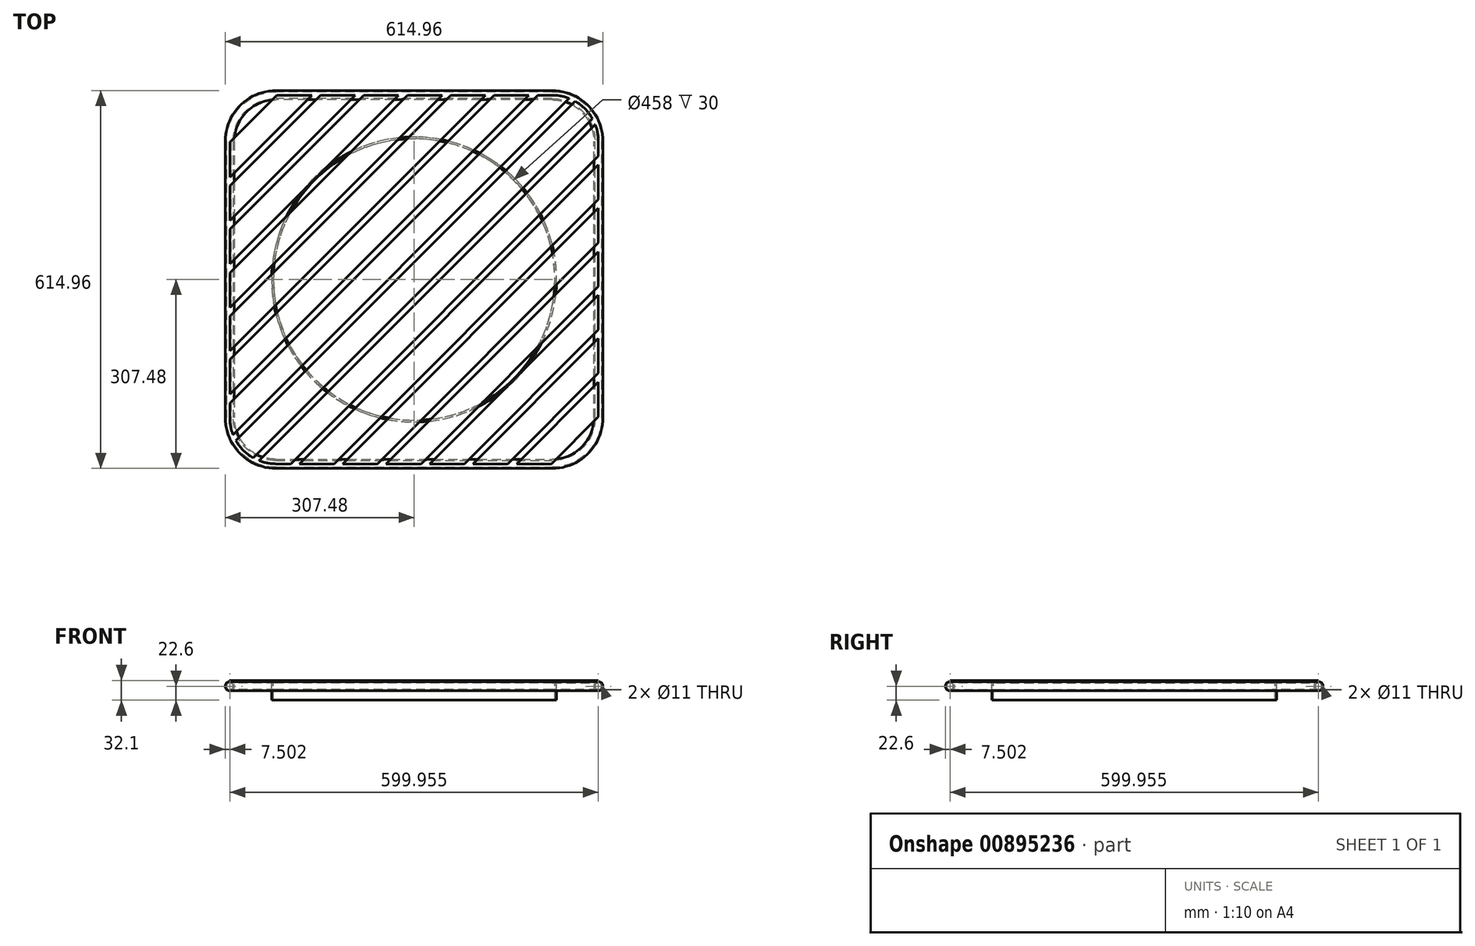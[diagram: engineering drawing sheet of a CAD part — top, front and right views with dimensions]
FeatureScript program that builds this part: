
annotation { "Feature Type Name" : "Feature", "Feature Type Description" : "" }
export const myFeature = defineFeature(function(context is Context, id is Id, definition is map)
    precondition{}
    {
        {
            var Q0;
            Q0=qCreatedBy(makeId("Top.planeOp"),FACE);
            var sketch = newSketch(context, id + "F0", { "sketchPlane" : qUnion([Q0])});
            skLineSegment(sketch, "E0.bottom", {"start": v(-225, 300) * mm, "end": v(225, 300) * mm});
            skLineSegment(sketch, "E0.top", {"start": v(-225, -300) * mm, "end": v(225, -300) * mm});
            skLineSegment(sketch, "E0.left", {"start": v(-300, 225) * mm, "end": v(-300, -225) * mm});
            skLineSegment(sketch, "E0.right", {"start": v(300, 225) * mm, "end": v(300, -225) * mm});
            skPoint(sketch, "E0.middle", {"position": v(0, 0) * mm});
            skArc(sketch, "E1", {"start": v(225, -300) * mm, "mid": v(278.03, -278.03) * mm, "end": v(300, -225) * mm});
            skPoint(sketch, "E2.orphan", {"position": v(300, -300) * mm});
            skArc(sketch, "E3", {"start": v(-300, -225) * mm, "mid": v(-278.03, -278.03) * mm, "end": v(-225, -300) * mm});
            skPoint(sketch, "E4.orphan", {"position": v(-300, -300) * mm});
            skArc(sketch, "E5.MirrorCS", {"start": v(225, 300) * mm, "mid": v(278.03, 278.03) * mm, "end": v(300, 225) * mm});
            skArc(sketch, "E6.MirrorCS", {"start": v(-300, 225) * mm, "mid": v(-278.03, 278.03) * mm, "end": v(-225, 300) * mm});
            skPoint(sketch, "E7.orphan", {"position": v(-300, 300) * mm});
            skPoint(sketch, "E8.orphan", {"position": v(300, 300) * mm});
            skSolve(sketch);
        }
        {
            var Q0;
            Q0=qCreatedBy(makeId("Front.planeOp"),FACE);
            var sketch = newSketch(context, id + "F1", { "sketchPlane" : qUnion([Q0])});
            skCircle(sketch, "E9", {"center": v(-299.98, 0) * mm, "radius": 7.5 * mm});
            skCircle(sketch, "E10", {"center": v(-299.98, 0) * mm, "radius": 5.5 * mm});
            skSolve(sketch);
        }
        {
            var Q0;
            Q0=makeQuery(id+"F1.imprint","IMPRINT",FACE,{"disambiguationData":[TD([[makeQuery(id+"F1.imprint","IMPRINT",EDGE,{"derivedFrom":sQuery(id+"F1.wireOp",EDGE,"E9")}),1.0]])]});
            var Q1;
            Q1=sQuery(id+"F0.wireOp",EDGE,"E3");
            var Q2;
            Q2=sQuery(id+"F0.wireOp",EDGE,"E0.left");
            var Q3;
            Q3=sQuery(id+"F0.wireOp",EDGE,"E6.MirrorCS");
            var Q4;
            Q4=sQuery(id+"F0.wireOp",EDGE,"E0.bottom");
            var Q5;
            Q5=sQuery(id+"F0.wireOp",EDGE,"E5.MirrorCS");
            var Q6;
            Q6=sQuery(id+"F0.wireOp",EDGE,"E0.right");
            var Q7;
            Q7=sQuery(id+"F0.wireOp",EDGE,"E1");
            var Q8;
            Q8=sQuery(id+"F0.wireOp",EDGE,"E0.top");
            sweep(context, id + "F2", {"profiles" : qUnion([Q0]), "path" : qUnion([Q1, Q2, Q3, Q4, Q5, Q6, Q7, Q8])});
        }
        {
            var Q0;
            Q0=qCreatedBy(makeId("Top.planeOp"),FACE);
            cPlane(context, id + "F3", {"entities" : qUnion([Q0]), "cplaneType" : CPlaneType.OFFSET, "offset" : 7.5 * mm, "width" : 150 * mm, "height" : 150 * mm});
        }
        {
            var Q0;
            Q0=qCreatedBy(id+"F3.planeOp",FACE);
            var sketch = newSketch(context, id + "F4", { "sketchPlane" : qUnion([Q0])});
            skLineSegment(sketch, "E11.bottom", {"start": v(-225, 300) * mm, "end": v(225, 300) * mm});
            skLineSegment(sketch, "E11.top", {"start": v(-225, -300) * mm, "end": v(225, -300) * mm});
            skLineSegment(sketch, "E11.left", {"start": v(-300, 225) * mm, "end": v(-300, -225) * mm});
            skLineSegment(sketch, "E11.right", {"start": v(300, 225) * mm, "end": v(300, -225) * mm});
            skPoint(sketch, "E11.middle", {"position": v(0, 0) * mm});
            skArc(sketch, "E12", {"start": v(-225, 300) * mm, "mid": v(-278.03, 278.03) * mm, "end": v(-300, 225) * mm});
            skArc(sketch, "E13", {"start": v(300, 225) * mm, "mid": v(278.03, 278.03) * mm, "end": v(225, 300) * mm});
            skPoint(sketch, "E14.orphan", {"position": v(-300, 300) * mm});
            skPoint(sketch, "E15.orphan", {"position": v(300, 300) * mm});
            skArc(sketch, "E16.MirrorCS", {"start": v(-225, -300) * mm, "mid": v(-278.03, -278.03) * mm, "end": v(-300, -225) * mm});
            skArc(sketch, "E17.MirrorCS", {"start": v(300, -225) * mm, "mid": v(278.03, -278.03) * mm, "end": v(225, -300) * mm});
            skPoint(sketch, "E18.orphan", {"position": v(-300, -300) * mm});
            skPoint(sketch, "E19.orphan", {"position": v(300, -300) * mm});
            skLineSegment(sketch, "E20", {"start": v(-300, 11.13) * mm, "end": v(-11.13, 300) * mm});
            skLineSegment(sketch, "E21", {"start": v(45.44, 300) * mm, "end": v(-300, -45.44) * mm});
            skLineSegment(sketch, "E22", {"start": v(59.58, 300) * mm, "end": v(-300, -59.58) * mm});
            skLineSegment(sketch, "E23", {"start": v(116.15, 300) * mm, "end": v(-300, -116.15) * mm});
            skLineSegment(sketch, "E24", {"start": v(130.3, 300) * mm, "end": v(-300, -130.3) * mm});
            skLineSegment(sketch, "E25", {"start": v(186.86, 300) * mm, "end": v(-300, -186.86) * mm});
            skLineSegment(sketch, "E26", {"start": v(201, 300) * mm, "end": v(-300, -201) * mm});
            skLineSegment(sketch, "E27", {"start": v(257.57, 300) * mm, "end": v(-300, -257.57) * mm});
            skLineSegment(sketch, "E28", {"start": v(-290.25, -261.97) * mm, "end": v(261.97, 290.25) * mm});
            skLineSegment(sketch, "E29.MirrorCS", {"start": v(-261.97, -290.25) * mm, "end": v(290.25, 261.97) * mm});
            skLineSegment(sketch, "E30.MirrorCS", {"start": v(294.82, 252.4) * mm, "end": v(-252.4, -294.82) * mm});
            skLineSegment(sketch, "E31.MirrorCS", {"start": v(300, 201) * mm, "end": v(-201, -300) * mm});
            skLineSegment(sketch, "E32.MirrorCS", {"start": v(300, 186.86) * mm, "end": v(-186.86, -300) * mm});
            skLineSegment(sketch, "E33.MirrorCS", {"start": v(300, 130.3) * mm, "end": v(-130.3, -300) * mm});
            skLineSegment(sketch, "E34.MirrorCS", {"start": v(300, 116.15) * mm, "end": v(-116.15, -300) * mm});
            skLineSegment(sketch, "E35.MirrorCS", {"start": v(300, 59.58) * mm, "end": v(-59.58, -300) * mm});
            skLineSegment(sketch, "E36.MirrorCS", {"start": v(300, 45.44) * mm, "end": v(-45.44, -300) * mm});
            skLineSegment(sketch, "E37.MirrorCS", {"start": v(11.13, -300) * mm, "end": v(300, -11.13) * mm});
            skLineSegment(sketch, "E38", {"start": v(300, -25.27) * mm, "end": v(25.27, -300) * mm});
            skLineSegment(sketch, "E39", {"start": v(300, -81.84) * mm, "end": v(81.84, -300) * mm});
            skLineSegment(sketch, "E40", {"start": v(300, -95.98) * mm, "end": v(95.98, -300) * mm});
            skLineSegment(sketch, "E41", {"start": v(-225, -225) * mm, "end": v(225, 225) * mm});
            skLineSegment(sketch, "E42", {"start": v(300, -152.55) * mm, "end": v(152.55, -300) * mm});
            skLineSegment(sketch, "E43.MirrorCS", {"start": v(-152.55, 300) * mm, "end": v(-300, 152.55) * mm});
            skLineSegment(sketch, "E44.MirrorCS", {"start": v(-95.98, 300) * mm, "end": v(-300, 95.98) * mm});
            skLineSegment(sketch, "E45.MirrorCS", {"start": v(-81.84, 300) * mm, "end": v(-300, 81.84) * mm});
            skLineSegment(sketch, "E46.MirrorCS", {"start": v(-25.27, 300) * mm, "end": v(-300, 25.27) * mm});
            skLineSegment(sketch, "E47", {"start": v(-166.7, 300) * mm, "end": v(-300, 166.7) * mm});
            skLineSegment(sketch, "E48", {"start": v(-223.26, 300) * mm, "end": v(-300, 223.26) * mm});
            skLineSegment(sketch, "E49.MirrorCS", {"start": v(300, -166.7) * mm, "end": v(166.7, -300) * mm});
            skLineSegment(sketch, "E50.MirrorCS", {"start": v(300, -223.26) * mm, "end": v(223.26, -300) * mm});
            skSolve(sketch);
        }
        {
            var Q0;
            {var subQ0=sQuery(id+"F4.wireOp",EDGE,"E20");Q0=makeQuery(id+"F4.imprint","IMPRINT",FACE,{"disambiguationData":[TD([[makeQuery(id+"F4.imprint","IMPRINT",EDGE,{"derivedFrom":subQ0}),-1.0]])]});}
            var Q1;
            {var subQ0=sQuery(id+"F4.wireOp",EDGE,"E22");Q1=makeQuery(id+"F4.imprint","IMPRINT",FACE,{"disambiguationData":[TD([[makeQuery(id+"F4.imprint","IMPRINT",EDGE,{"derivedFrom":subQ0}),1.0]])]});}
            var Q2;
            {var subQ0=sQuery(id+"F4.wireOp",EDGE,"E24");Q2=makeQuery(id+"F4.imprint","IMPRINT",FACE,{"disambiguationData":[TD([[makeQuery(id+"F4.imprint","IMPRINT",EDGE,{"derivedFrom":subQ0}),1.0]])]});}
            var Q3;
            {var subQ0=sQuery(id+"F4.wireOp",EDGE,"E26");Q3=makeQuery(id+"F4.imprint","IMPRINT",FACE,{"disambiguationData":[TD([[makeQuery(id+"F4.imprint","IMPRINT",EDGE,{"derivedFrom":subQ0}),1.0]])]});}
            var Q4;
            {var subQ0=sQuery(id+"F4.wireOp",EDGE,"f3e3acb9-5dc7-480f-a169-b6047dde436d0.MirrorCS");Q4=makeQuery(id+"F4.imprint","IMPRINT",FACE,{"disambiguationData":[TD([[makeQuery(id+"F4.imprint","IMPRINT",EDGE,{"derivedFrom":subQ0}),1.0]])]});}
            var Q5;
            {var subQ0=sQuery(id+"F4.wireOp",EDGE,"8c5f72dc-6430-4fd1-9669-a3bc66972e370.MirrorCS");Q5=makeQuery(id+"F4.imprint","IMPRINT",FACE,{"disambiguationData":[TD([[makeQuery(id+"F4.imprint","IMPRINT",EDGE,{"derivedFrom":subQ0}),1.0]])]});}
            var Q6;
            {var subQ0=sQuery(id+"F4.wireOp",EDGE,"5638e17f-524b-40a8-8cfa-9c4565ae56270.MirrorCS");Q6=makeQuery(id+"F4.imprint","IMPRINT",FACE,{"disambiguationData":[TD([[makeQuery(id+"F4.imprint","IMPRINT",EDGE,{"derivedFrom":subQ0}),1.0]])]});}
            var Q7;
            {var subQ0=sQuery(id+"F4.wireOp",EDGE,"d3d81764-08a6-4486-8bd4-b46154aa33660.MirrorCS");Q7=makeQuery(id+"F4.imprint","IMPRINT",FACE,{"disambiguationData":[TD([[makeQuery(id+"F4.imprint","IMPRINT",EDGE,{"derivedFrom":subQ0}),1.0]])]});}
            var Q8;
            {var subQ0=sQuery(id+"F4.wireOp",EDGE,"Kz8hN87C-jPTE-dKEJ-GhUn-43Xg0fKDj0rT");Q8=makeQuery(id+"F4.imprint","IMPRINT",FACE,{"disambiguationData":[TD([[makeQuery(id+"F4.imprint","IMPRINT",EDGE,{"derivedFrom":subQ0}),-1.0]])]});}
            var Q9;
            {var subQ0=sQuery(id+"F4.wireOp",EDGE,"E30.MirrorCS");Q9=makeQuery(id+"F4.imprint","IMPRINT",FACE,{"disambiguationData":[TD([[makeQuery(id+"F4.imprint","IMPRINT",EDGE,{"derivedFrom":subQ0}),1.0]])]});}
            var Q10;
            {var subQ0=sQuery(id+"F4.wireOp",EDGE,"E32.MirrorCS");Q10=makeQuery(id+"F4.imprint","IMPRINT",FACE,{"disambiguationData":[TD([[makeQuery(id+"F4.imprint","IMPRINT",EDGE,{"derivedFrom":subQ0}),1.0]])]});}
            var Q11;
            {var subQ0=sQuery(id+"F4.wireOp",EDGE,"E34.MirrorCS");Q11=makeQuery(id+"F4.imprint","IMPRINT",FACE,{"disambiguationData":[TD([[makeQuery(id+"F4.imprint","IMPRINT",EDGE,{"derivedFrom":subQ0}),1.0]])]});}
            var Q12;
            {var subQ0=sQuery(id+"F4.wireOp",EDGE,"E36.MirrorCS");Q12=makeQuery(id+"F4.imprint","IMPRINT",FACE,{"disambiguationData":[TD([[makeQuery(id+"F4.imprint","IMPRINT",EDGE,{"derivedFrom":subQ0}),1.0]])]});}
            var Q13;
            {var subQ0=sQuery(id+"F4.wireOp",EDGE,"E38");Q13=makeQuery(id+"F4.imprint","IMPRINT",FACE,{"disambiguationData":[TD([[makeQuery(id+"F4.imprint","IMPRINT",EDGE,{"derivedFrom":subQ0}),1.0]])]});}
            var Q14;
            {var subQ6=sQuery(id+"F4.wireOp",EDGE,"E40");Q14=makeQuery(id+"F4.imprint","IMPRINT",FACE,{"disambiguationData":[TD([[makeQuery(id+"F4.imprint","IMPRINT",EDGE,{"derivedFrom":subQ6}),1.0]])]});}
            var Q15;
            {var subQ0=sQuery(id+"F4.wireOp",EDGE,"E45.MirrorCS");Q15=makeQuery(id+"F4.imprint","IMPRINT",FACE,{"disambiguationData":[TD([[makeQuery(id+"F4.imprint","IMPRINT",EDGE,{"derivedFrom":subQ0}),1.0]])]});}
            var Q16;
            {var subQ3=sQuery(id+"F4.wireOp",EDGE,"E43.MirrorCS");Q16=makeQuery(id+"F4.imprint","IMPRINT",FACE,{"disambiguationData":[TD([[makeQuery(id+"F4.imprint","IMPRINT",EDGE,{"derivedFrom":subQ3}),1.0]])]});}
            var Q17;
            {var subQ0=sQuery(id+"F4.wireOp",EDGE,"E28");Q17=makeQuery(id+"F4.imprint","IMPRINT",FACE,{"disambiguationData":[TD([[makeQuery(id+"F4.imprint","IMPRINT",EDGE,{"derivedFrom":subQ0}),-1.0]])]});}
            var Q18;
            {var subQ7=sQuery(id+"F4.wireOp",EDGE,"E49.MirrorCS");Q18=makeQuery(id+"F4.imprint","IMPRINT",FACE,{"disambiguationData":[TD([[makeQuery(id+"F4.imprint","IMPRINT",EDGE,{"derivedFrom":subQ7}),1.0]])]});}
            var Q19;
            {var subQ8=sQuery(id+"F4.wireOp",EDGE,"E47");Q19=makeQuery(id+"F4.imprint","IMPRINT",FACE,{"disambiguationData":[TD([[makeQuery(id+"F4.imprint","IMPRINT",EDGE,{"derivedFrom":subQ8}),-1.0]])]});}
            extrude(context, id + "F5", {"entities" : qUnion([Q0, Q1, Q2, Q3, Q4, Q5, Q6, Q7, Q8, Q9, Q10, Q11, Q12, Q13, Q14, Q15, Q16, Q17, Q18, Q19]), "operationType" : NewBodyOperationType.ADD, "depth" : 2 * mm, "offsetDistance" : 25 * mm, "hasSecondDirection" : true, "secondDirectionOppositeDirection" : true, "secondDirectionDepth" : .1 * mm});
        }
        {
            var Q0;
            Q0=makeQuery(id+"F5.opExtrude","CAP_FACE",FACE,{"disambiguationData":[OSD([sQuery(id+"F4.wireOp",EDGE,"E11.top"),sQuery(id+"F4.wireOp",EDGE,"E11.right"),sQuery(id+"F4.wireOp",EDGE,"E34.MirrorCS"),sQuery(id+"F4.wireOp",EDGE,"E35.MirrorCS")])],"isStart":true});
            var sketch = newSketch(context, id + "F6", { "sketchPlane" : qUnion([Q0])});
            skCircle(sketch, "E51", {"center": v(0, 0) * mm, "radius": 229 * mm});
            skCircle(sketch, "E52", {"center": v(0, 0) * mm, "radius": 232 * mm});
            skSolve(sketch);
        }
        {
            var Q0;
            Q0=qSketchRegion(id+"F6",true);
            extrude(context, id + "F7", {"entities" : qUnion([Q0]), "operationType" : NewBodyOperationType.ADD, "depth" : 30 * mm, "offsetDistance" : 25 * mm});
        }
    });
